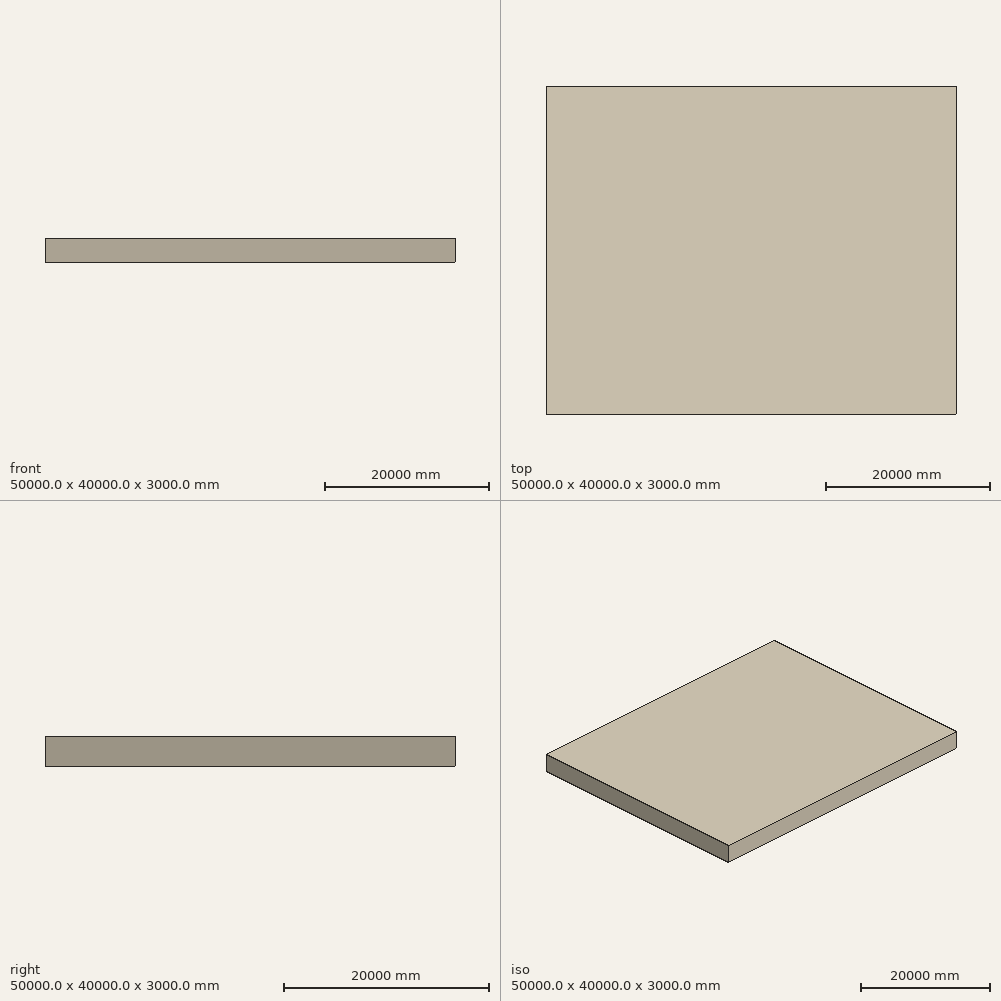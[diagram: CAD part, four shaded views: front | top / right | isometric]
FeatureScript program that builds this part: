
annotation { "Feature Type Name" : "Feature", "Feature Type Description" : "" }
export const myFeature = defineFeature(function(context is Context, id is Id, definition is map)
    precondition{}
    {
        {
            var Q0;
            Q0=qCreatedBy(makeId("Top.planeOp"),FACE);
            var sketch = newSketch(context, id + "F0", { "sketchPlane" : qUnion([Q0])});
            skLineSegment(sketch, "E0.bottom", {"start": v(0, 0) * mm, "end": v(-50000, 0) * mm});
            skLineSegment(sketch, "E0.top", {"start": v(0, -40000) * mm, "end": v(-50000, -40000) * mm});
            skLineSegment(sketch, "E0.left", {"start": v(0, 0) * mm, "end": v(0, -40000) * mm});
            skLineSegment(sketch, "E0.right", {"start": v(-50000, 0) * mm, "end": v(-50000, -40000) * mm});
            skSolve(sketch);
        }
        {
            var Q0;
            Q0=makeQuery(id+"F0.imprint","IMPRINT",FACE,{"disambiguationData":[TD([[makeQuery(id+"F0.imprint","IMPRINT",EDGE,{"derivedFrom":sQuery(id+"F0.wireOp",EDGE,"E0.bottom")}),1.0]])]});
            extrude(context, id + "F1", {"entities" : qUnion([Q0]), "depth" : 3000 * mm, "offsetDistance" : 25 * mm});
        }
    });
